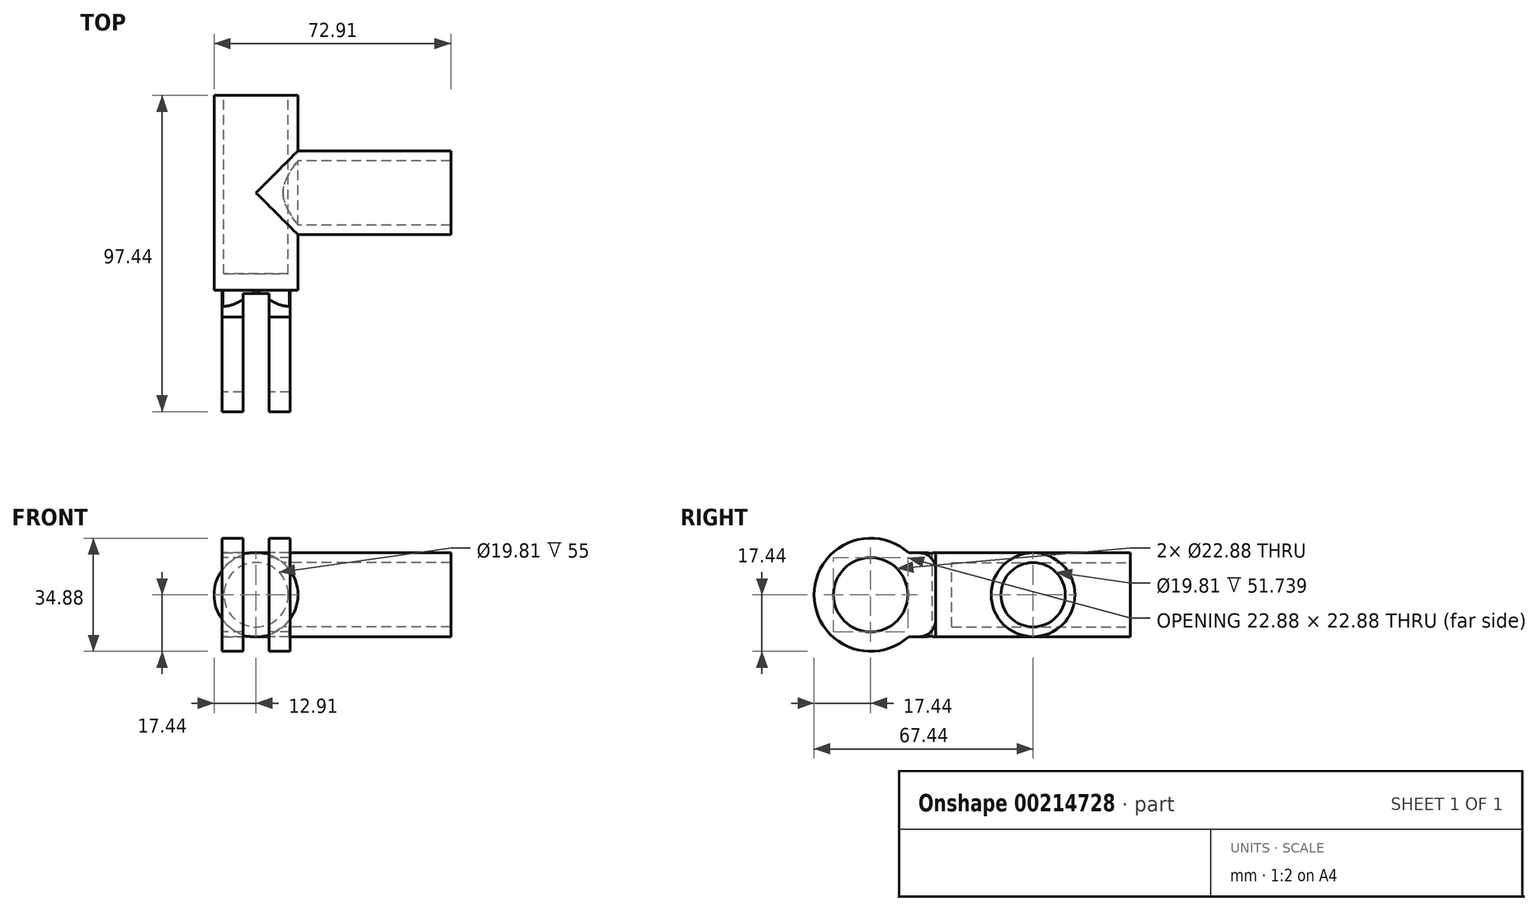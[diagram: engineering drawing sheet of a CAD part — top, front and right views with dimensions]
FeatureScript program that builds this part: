
annotation { "Feature Type Name" : "Feature", "Feature Type Description" : "" }
export const myFeature = defineFeature(function(context is Context, id is Id, definition is map)
    precondition{}
    {
        {
            assignVariable(context, id + "F0", {"name" : "ZZW", "anyValue" : 7});
        }
        {
            var Q0;
            Q0=qCreatedBy(makeId("Front.planeOp"),FACE);
            var sketch = newSketch(context, id + "F1", { "sketchPlane" : qUnion([Q0])});
            skCircle(sketch, "E0", {"center": v(0, 0) * mm, "radius": 9.9 * mm});
            skCircle(sketch, "E1", {"center": v(0, 0) * mm, "radius": 12.9 * mm});
            skSolve(sketch);
        }
        {
            var Q0;
            Q0=qSketchRegion(id+"F1",true);
            extrude(context, id + "F2", {"entities" : qUnion([Q0]), "depth" : 55 * mm});
        }
        {
            var Q0;
            Q0=makeQuery(id+"F2.opExtrude","CAP_FACE",FACE,{"disambiguationData":[OSD([sQuery(id+"F1.wireOp",EDGE,"E0"),sQuery(id+"F1.wireOp",EDGE,"E1")])],"isStart":false});
            var sketch = newSketch(context, id + "F3", { "sketchPlane" : qUnion([Q0])});
            skCircle(sketch, "E2", {"center": v(0, 0) * mm, "radius": 12.9 * mm});
            skSolve(sketch);
        }
        {
            var Q0;
            Q0=qSketchRegion(id+"F3",true);
            extrude(context, id + "F4", {"entities" : qUnion([Q0]), "operationType" : NewBodyOperationType.ADD, "depth" : 5 * mm});
        }
        {
            var Q0;
            Q0=qCreatedBy(makeId("Right.planeOp"),FACE);
            var sketch = newSketch(context, id + "F5", { "sketchPlane" : qUnion([Q0])});
            skLineSegment(sketch, "E3", {"start": v(0, 0) * mm, "end": v(0, -12.9) * mm, "construction": true});
            skLineSegment(sketch, "E4", {"start": v(0, -12.9) * mm, "end": v(-60, -12.9) * mm, "construction": true});
            skLineSegment(sketch, "E5", {"start": v(-60, 0) * mm, "end": v(-60, 12.9) * mm, "construction": true});
            skLineSegment(sketch, "E6", {"start": v(-60, -12.9) * mm, "end": v(-80, -12.9) * mm});
            skLineSegment(sketch, "E7", {"start": v(-80, -12.9) * mm, "end": v(-80, 12.9) * mm});
            skLineSegment(sketch, "E8", {"start": v(-80, 12.9) * mm, "end": v(-60, 12.9) * mm});
            skLineSegment(sketch, "E9", {"start": v(-60, -12.9) * mm, "end": v(-60, 12.9) * mm});
            skCircle(sketch, "E10", {"center": v(-80, 0) * mm, "radius": 11.44 * mm});
            skCircle(sketch, "E11", {"center": v(-80, 0) * mm, "radius": 17.44 * mm});
            skSolve(sketch);
        }
        {
            var Q0;
            {var subQ1=sQuery(id+"F5.wireOp",EDGE,"E7");var subQ5=sQuery(id+"F5.wireOp",EDGE,"E6");var subQ6=makeQuery(id+"F5.imprint","INTERSECT",VERTEX,{"derivedFrom":[subQ5,subQ1]});Q0=makeQuery(id+"F5.imprint","IMPRINT",FACE,{"disambiguationData":[TD([[makeQuery(id+"F5.imprint","IMPRINT",EDGE,{"disambiguationData":[TD([[subQ6,1.0]])],"derivedFrom":subQ5}),1.0]])]});}
            var Q1;
            {var subQ0=sQuery(id+"F5.wireOp",EDGE,"E9");Q1=makeQuery(id+"F5.imprint","IMPRINT",FACE,{"disambiguationData":[TD([[makeQuery(id+"F5.imprint","IMPRINT",EDGE,{"derivedFrom":subQ0}),1.0]])]});}
            var Q2;
            {var subQ1=sQuery(id+"F5.wireOp",EDGE,"E7");var subQ5=sQuery(id+"F5.wireOp",EDGE,"E6");var subQ6=makeQuery(id+"F5.imprint","INTERSECT",VERTEX,{"derivedFrom":[subQ5,subQ1]});Q2=makeQuery(id+"F5.imprint","IMPRINT",FACE,{"disambiguationData":[TD([[makeQuery(id+"F5.imprint","IMPRINT",EDGE,{"disambiguationData":[TD([[subQ6,1.0]])],"derivedFrom":subQ5}),-1.0]])]});}
            extrude(context, id + "F6", {"entities" : qUnion([Q0, Q1, Q2]), "operationType" : NewBodyOperationType.ADD, "depth" : (getVariable(context, 'ZZW')) * 3 / 2 * mm, "hasSecondDirection" : true, "secondDirectionOppositeDirection" : true, "secondDirectionDepth" : (getVariable(context, 'ZZW')) * 3 / 2 * mm});
        }
        {
            var Q0;
            Q0=qCreatedBy(makeId("Right.planeOp"),FACE);
            var sketch = newSketch(context, id + "F7", { "sketchPlane" : qUnion([Q0])});
            skCircle(sketch, "E12", {"center": v(-30, 0) * mm, "radius": 9.9 * mm});
            skCircle(sketch, "E13", {"center": v(-30, 0) * mm, "radius": 12.9 * mm});
            skSolve(sketch);
        }
        {
            var Q0;
            Q0=qSketchRegion(id+"F7",true);
            extrude(context, id + "F8", {"entities" : qUnion([Q0]), "operationType" : NewBodyOperationType.ADD, "depth" : 60 * mm});
        }
        {
            var Q0;
            Q0=makeQuery(id+"F4.opExtrude","CAP_FACE",FACE,{"disambiguationData":[OSD([sQuery(id+"F3.wireOp",EDGE,"E2")])],"isStart":true});
            var sketch = newSketch(context, id + "F9", { "sketchPlane" : qUnion([Q0])});
            skCircle(sketch, "E14", {"center": v(0, 0) * mm, "radius": 9.9 * mm});
            skSolve(sketch);
        }
        {
            var Q0;
            Q0=qSketchRegion(id+"F9",true);
            extrude(context, id + "F10", {"entities" : qUnion([Q0]), "operationType" : NewBodyOperationType.REMOVE, "depth" : 60 * mm});
        }
        {
            var Q0;
            Q0=qCreatedBy(makeId("Top.planeOp"),FACE);
            var sketch = newSketch(context, id + "F11", { "sketchPlane" : qUnion([Q0])});
            skLineSegment(sketch, "E15", {"start": v(0, 0) * mm, "end": v(0, -60) * mm});
            skLineSegment(sketch, "E16", {"start": v(0, -60) * mm, "end": v(-4, -60) * mm, "construction": true});
            skLineSegment(sketch, "E17", {"start": v(0, -60) * mm, "end": v(4, -60) * mm, "construction": true});
            skLineSegment(sketch, "E18", {"start": v(-4, -60) * mm, "end": v(-4, -61) * mm, "construction": true});
            skLineSegment(sketch, "E19.bottom", {"start": v(-4, -61) * mm, "end": v(4, -61) * mm});
            skLineSegment(sketch, "E19.top", {"start": v(-4, -98.79) * mm, "end": v(4, -98.79) * mm});
            skLineSegment(sketch, "E19.left", {"start": v(-4, -61) * mm, "end": v(-4, -98.79) * mm});
            skLineSegment(sketch, "E19.right", {"start": v(4, -61) * mm, "end": v(4, -98.79) * mm});
            skSolve(sketch);
        }
        {
            var Q0;
            Q0=makeQuery(id+"F11.imprint","IMPRINT",FACE,{"disambiguationData":[TD([[makeQuery(id+"F11.imprint","IMPRINT",EDGE,{"derivedFrom":sQuery(id+"F11.wireOp",EDGE,"E19.bottom")}),-1.0]])]});
            extrude(context, id + "F12", {"entities" : qUnion([Q0]), "operationType" : NewBodyOperationType.REMOVE, "oppositeDirection" : true, "depth" : 25 * mm, "hasSecondDirection" : true, "secondDirectionOppositeDirection" : false, "secondDirectionDepth" : 25 * mm});
        }
        {
            var Q0;
            {var subQ0=sQuery(id+"F5.wireOp",EDGE,"E9");var subQ1=sQuery(id+"F5.wireOp",EDGE,"E8");Q0=makeQuery(id+"F6.boolean.opBoolean","SPLIT",EDGE,{"disambiguationData":[TD([makeQuery(id+"F6.opExtrude","CAP_FACE",FACE,{"disambiguationData":[OSD([sQuery(id+"F5.wireOp",EDGE,"E6"),subQ1,subQ0,sQuery(id+"F5.wireOp",EDGE,"E10"),sQuery(id+"F5.wireOp",EDGE,"E11")])],"isStart":false})])],"derivedFrom":makeQuery(id+"F6.opExtrude","SWEPT_EDGE",EDGE,{"disambiguationData":[OSD([subQ1,subQ0])]})});}
            var Q1;
            {var subQ0=sQuery(id+"F5.wireOp",EDGE,"E6");var subQ1=sQuery(id+"F5.wireOp",EDGE,"E9");Q1=makeQuery(id+"F6.boolean.opBoolean","SPLIT",EDGE,{"disambiguationData":[TD([makeQuery(id+"F6.opExtrude","CAP_FACE",FACE,{"disambiguationData":[OSD([subQ0,sQuery(id+"F5.wireOp",EDGE,"E8"),subQ1,sQuery(id+"F5.wireOp",EDGE,"E10"),sQuery(id+"F5.wireOp",EDGE,"E11")])],"isStart":false})])],"derivedFrom":makeQuery(id+"F6.opExtrude","SWEPT_EDGE",EDGE,{"disambiguationData":[OSD([subQ0,subQ1])]})});}
            var Q2;
            {var subQ0=sQuery(id+"F5.wireOp",EDGE,"E9");var subQ1=sQuery(id+"F5.wireOp",EDGE,"E6");Q2=makeQuery(id+"F6.boolean.opBoolean","SPLIT",EDGE,{"disambiguationData":[TD([makeQuery(id+"F6.opExtrude","CAP_FACE",FACE,{"disambiguationData":[OSD([subQ1,sQuery(id+"F5.wireOp",EDGE,"E8"),subQ0,sQuery(id+"F5.wireOp",EDGE,"E10"),sQuery(id+"F5.wireOp",EDGE,"E11")])],"isStart":true})])],"derivedFrom":makeQuery(id+"F6.opExtrude","SWEPT_EDGE",EDGE,{"disambiguationData":[OSD([subQ1,subQ0])]})});}
            fillet(context, id + "F13", {"entities" : qUnion([Q0, Q1, Q2]), "radius" : 5 * mm, "tangentPropagation" : true, "allowEdgeOverflow" : false});
        }
    });
